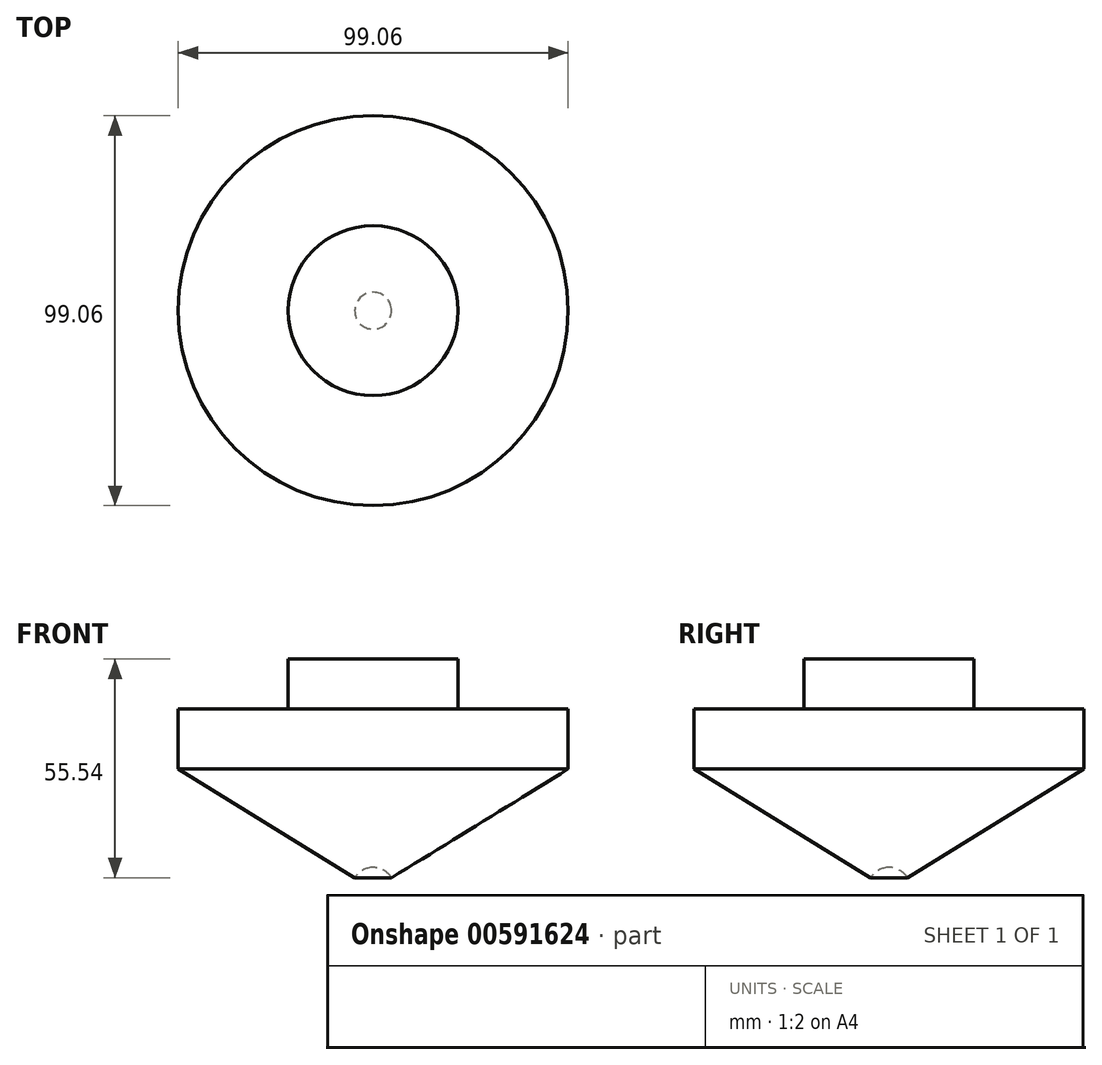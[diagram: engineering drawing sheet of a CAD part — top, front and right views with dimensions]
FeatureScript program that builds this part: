
annotation { "Feature Type Name" : "Feature", "Feature Type Description" : "" }
export const myFeature = defineFeature(function(context is Context, id is Id, definition is map)
    precondition{}
    {
        {
            var Q0;
            Q0=qCreatedBy(makeId("Front.planeOp"),FACE);
            var sketch = newSketch(context, id + "F0", { "sketchPlane" : qUnion([Q0])});
            skLineSegment(sketch, "E0", {"start": v(0, 0) * mm, "end": v(49.53, 30.48) * mm});
            skLineSegment(sketch, "E1", {"start": v(49.53, 30.48) * mm, "end": v(49.53, 45.72) * mm});
            skLineSegment(sketch, "E2", {"start": v(49.53, 45.72) * mm, "end": v(21.59, 45.72) * mm});
            skLineSegment(sketch, "E3", {"start": v(21.6, 45.72) * mm, "end": v(21.6, 58.42) * mm});
            skLineSegment(sketch, "E4", {"start": v(21.59, 58.42) * mm, "end": v(0, 58.42) * mm});
            skLineSegment(sketch, "E5", {"start": v(0, 58.42) * mm, "end": v(0, 0) * mm});
            skCircle(sketch, "E6", {"center": v(0, 0) * mm, "radius": 5.5 * mm});
            skSolve(sketch);
        }
        {
            var Q0;
            {var subQ0=sQuery(id+"F0.wireOp",EDGE,"E1");Q0=makeQuery(id+"F0.imprint","IMPRINT",FACE,{"disambiguationData":[TD([[makeQuery(id+"F0.imprint","IMPRINT",EDGE,{"derivedFrom":subQ0}),1.0]])]});}
            var Q1;
            Q1=sQuery(id+"F0.wireOp",EDGE,"E5");
            revolve(context, id + "F1", {"entities" : qUnion([Q0]), "axis" : qUnion([Q1]), "revolveType" : RevolveType.FULL});
        }
    });
